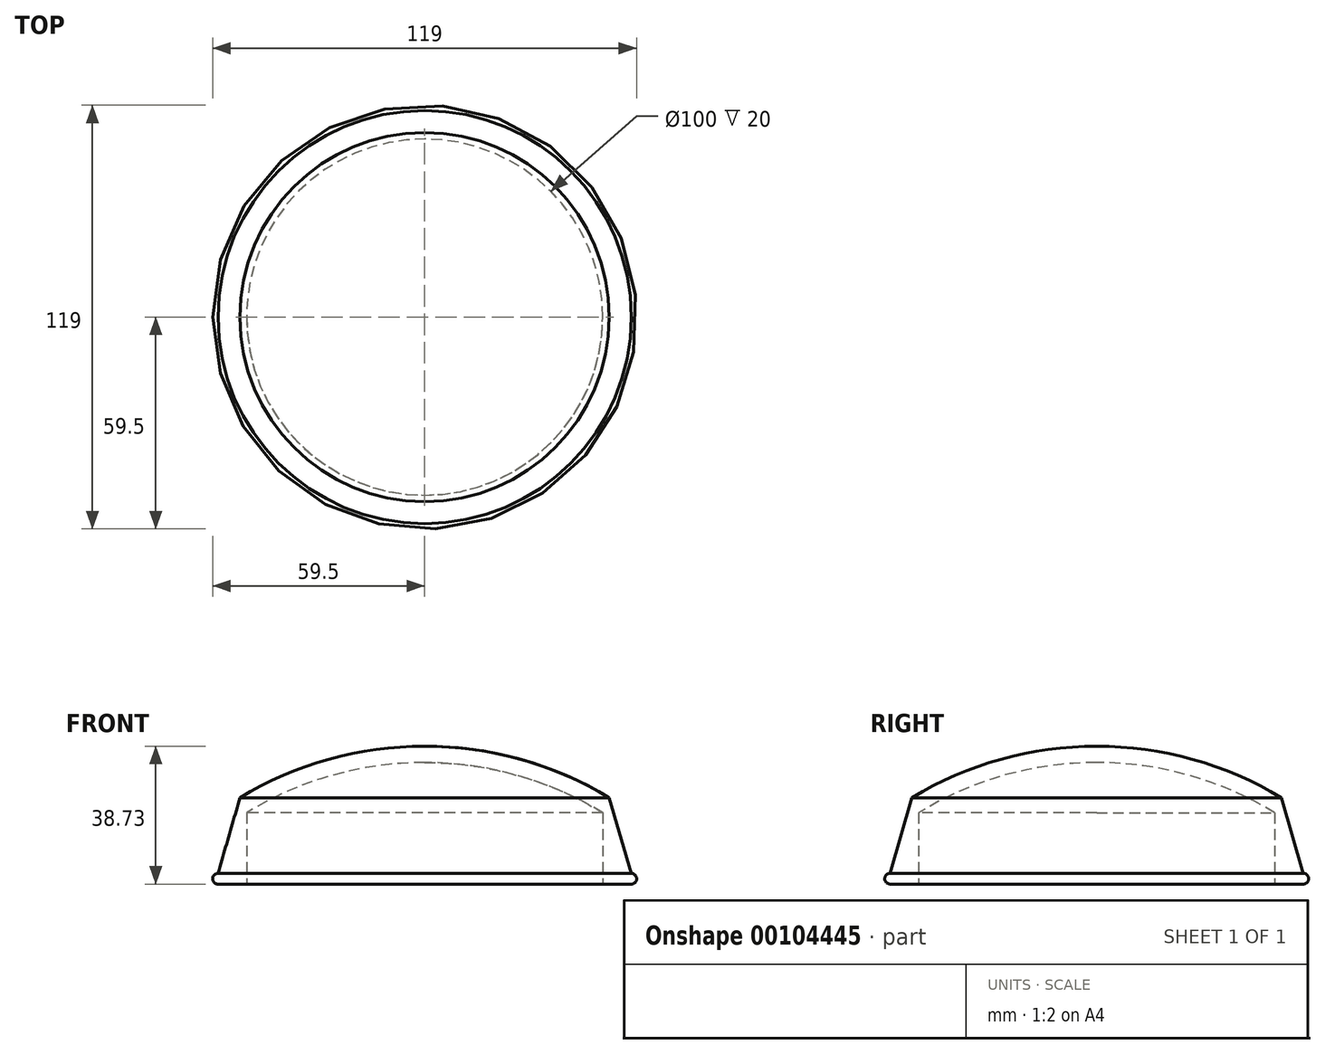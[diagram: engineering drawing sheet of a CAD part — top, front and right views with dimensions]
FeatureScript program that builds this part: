
annotation { "Feature Type Name" : "Feature", "Feature Type Description" : "" }
export const myFeature = defineFeature(function(context is Context, id is Id, definition is map)
    precondition{}
    {
        {
            var Q0;
            Q0=qCreatedBy(makeId("Front.planeOp"),FACE);
            var sketch = newSketch(context, id + "F0", { "sketchPlane" : qUnion([Q0])});
            skLineSegment(sketch, "E0", {"start": v(0, 0) * mm, "end": v(50, 0) * mm, "construction": true});
            skLineSegment(sketch, "E1", {"start": v(50, 0) * mm, "end": v(58, 0) * mm});
            skLineSegment(sketch, "E2", {"start": v(58, 0) * mm, "end": v(58, 3) * mm, "construction": true});
            skArc(sketch, "E3", {"start": v(58, 0) * mm, "mid": v(59.5, 1.5) * mm, "end": v(58, 3) * mm});
            skLineSegment(sketch, "E4", {"start": v(50, 0) * mm, "end": v(50, 20) * mm});
            skLineSegment(sketch, "E5", {"start": v(58, 3) * mm, "end": v(51.83, 24.25) * mm});
            skLineSegment(sketch, "E6", {"start": v(51.83, 24.25) * mm, "end": v(50, 20) * mm, "construction": true});
            skLineSegment(sketch, "E7", {"start": v(0, 0) * mm, "end": v(0, 34.15) * mm, "construction": true});
            skLineSegment(sketch, "E8", {"start": v(0, 34.15) * mm, "end": v(0, 38.73) * mm});
            skLineSegment(sketch, "E9", {"start": v(0, 0) * mm, "end": v(0, -61.27) * mm, "construction": true});
            skArc(sketch, "E10", {"start": v(51.83, 24.25) * mm, "mid": v(26.9, 35.05) * mm, "end": v(0, 38.73) * mm});
            skArc(sketch, "E11", {"start": v(50, 20) * mm, "mid": v(25.98, 30.54) * mm, "end": v(0, 34.15) * mm});
            skSolve(sketch);
        }
        {
            var Q0;
            Q0 = qSketchRegion(id + "F0", true);
            var Q1;
            Q1=sQuery(id+"F0.wireOp",EDGE,"E7");
            revolve(context, id + "F1", {"entities" : qUnion([Q0]), "axis" : qUnion([Q1]), "revolveType" : RevolveType.FULL});
        }
    });
